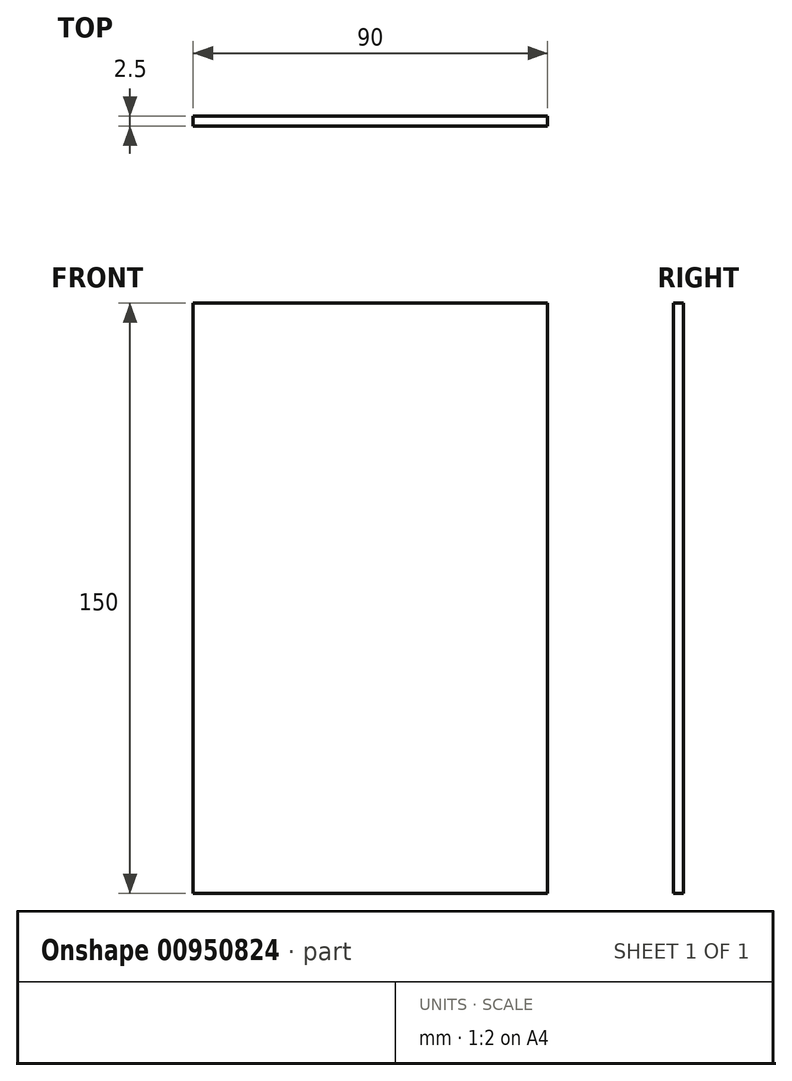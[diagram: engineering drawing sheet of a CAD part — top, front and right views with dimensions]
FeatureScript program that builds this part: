
annotation { "Feature Type Name" : "Feature", "Feature Type Description" : "" }
export const myFeature = defineFeature(function(context is Context, id is Id, definition is map)
    precondition{}
    {
        {
            var Q0;
            Q0=qCreatedBy(makeId("Front.planeOp"),FACE);
            var sketch = newSketch(context, id + "F0", { "sketchPlane" : qUnion([Q0])});
            skLineSegment(sketch, "E0.bottom", {"start": v(45, 75) * mm, "end": v(-45, 75) * mm});
            skLineSegment(sketch, "E0.top", {"start": v(45, -75) * mm, "end": v(-45, -75) * mm});
            skLineSegment(sketch, "E0.left", {"start": v(45, 75) * mm, "end": v(45, -75) * mm});
            skLineSegment(sketch, "E0.right", {"start": v(-45, 75) * mm, "end": v(-45, -75) * mm});
            skPoint(sketch, "E0.middle", {"position": v(0, 0) * mm});
            skSolve(sketch);
        }
        {
            var Q0;
            Q0=qSketchRegion(id+"F0",true);
            extrude(context, id + "F1", {"entities" : qUnion([Q0]), "depth" : 2.5 * mm, "offsetDistance" : 25 * mm});
        }
    });
